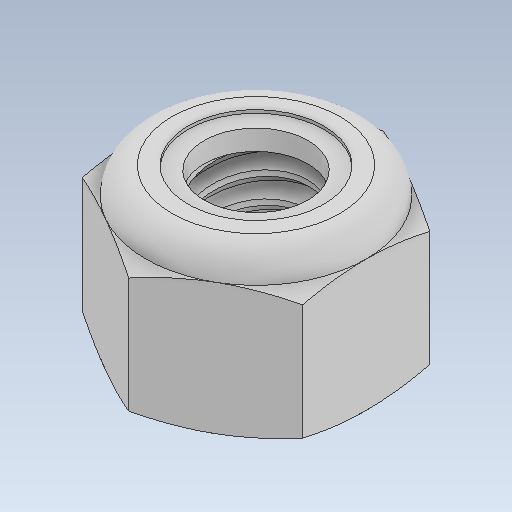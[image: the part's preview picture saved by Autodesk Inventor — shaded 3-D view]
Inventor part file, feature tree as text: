
AUTODESK INVENTOR PART (.ipt)
format: ipt  version: 2020 (Build 240168000, 168)  size: 299,520 bytes
history: native  units: in
note: dims shown in document units (in); Inventor stores cm internally (conversion verified against a paired STEP export)
features: other x1, revolve x1
ambient origin geometry x8: Origin, YZ Plane, XZ Plane, XY Plane, X Axis, Y Axis, Z Axis, Center Point
bodies: Solid1 (feature_tree), Solid2 (feature_tree)
feature tree (2):
  other  "Cut-Revolve4"
  revolve  "Revolve2"  [1 undecoded]
note: 1 required parameter value undecoded (feature->parameter linkage not recoverable at this tier; creation-order binding heuristic only, values carry confidence <= 0.55)
